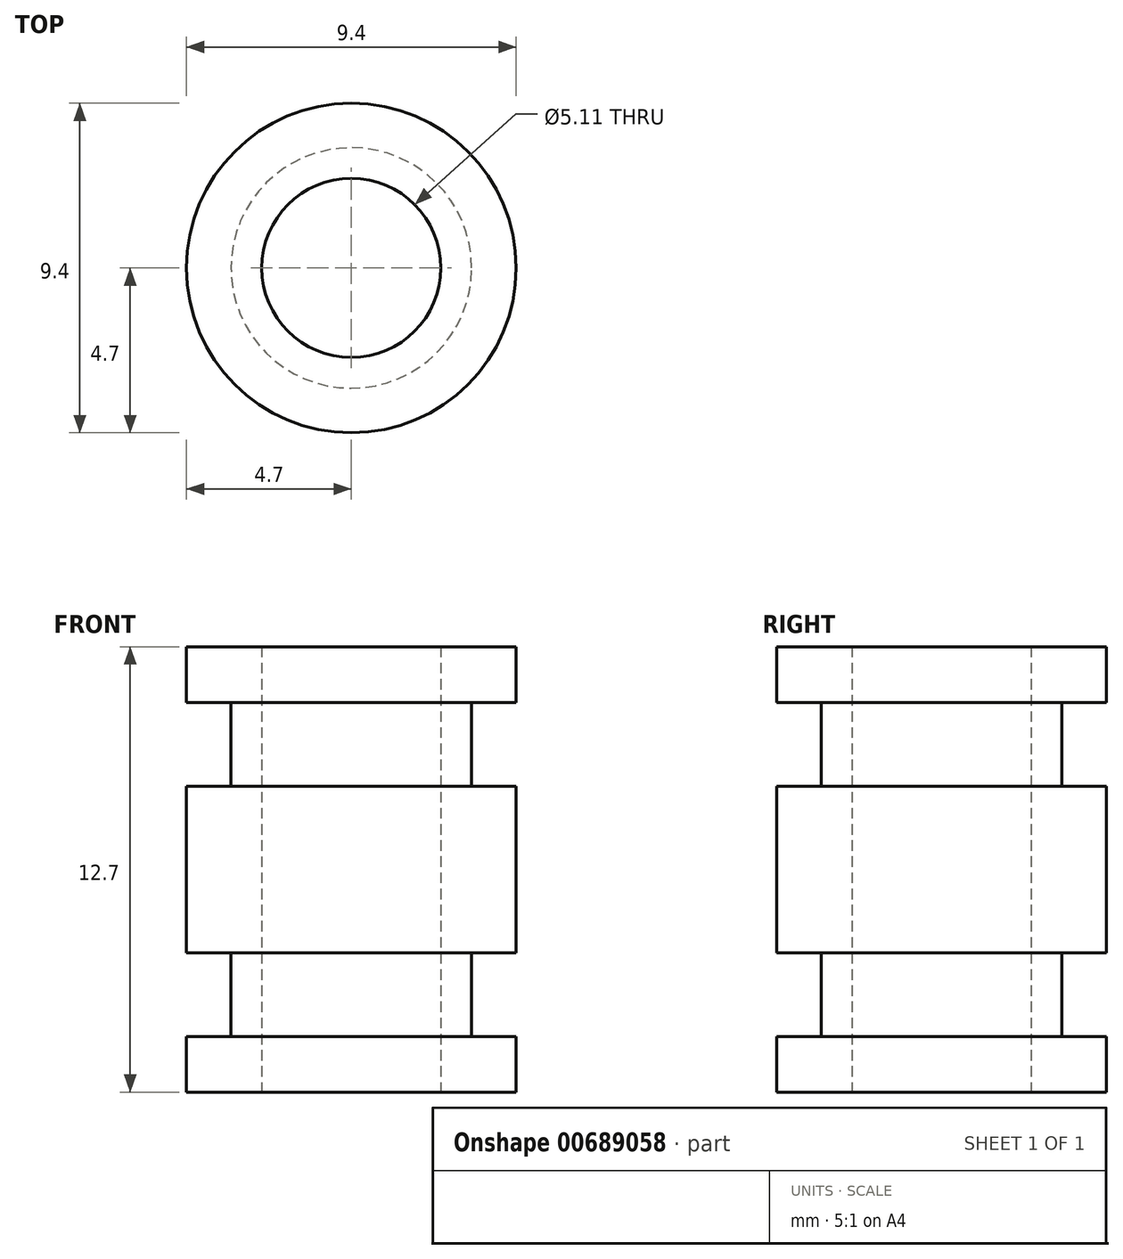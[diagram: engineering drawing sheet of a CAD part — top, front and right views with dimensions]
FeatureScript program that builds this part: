
annotation { "Feature Type Name" : "Feature", "Feature Type Description" : "" }
export const myFeature = defineFeature(function(context is Context, id is Id, definition is map)
    precondition{}
    {
        {
            var Q0;
            Q0=qCreatedBy(makeId("Front.planeOp"),FACE);
            var sketch = newSketch(context, id + "F0", { "sketchPlane" : qUnion([Q0])});
            skPoint(sketch, "E0", {"position": v(0, 6.35) * mm});
            skLineSegment(sketch, "E1", {"start": v(0, 6.35) * mm, "end": v(24.5, 6.35) * mm, "construction": true});
            skLineSegment(sketch, "E2", {"start": v(0, 6.35) * mm, "end": v(0, 0) * mm});
            skLineSegment(sketch, "E3", {"start": v(0, 0) * mm, "end": v(4.7, 0) * mm});
            skLineSegment(sketch, "E4", {"start": v(4.7, 0) * mm, "end": v(4.7, 1.59) * mm});
            skLineSegment(sketch, "E5", {"start": v(4.7, 1.59) * mm, "end": v(3.43, 1.59) * mm});
            skLineSegment(sketch, "E6", {"start": v(3.43, 1.59) * mm, "end": v(3.43, 3.98) * mm});
            skLineSegment(sketch, "E7", {"start": v(3.43, 3.98) * mm, "end": v(4.7, 3.98) * mm});
            skLineSegment(sketch, "E8", {"start": v(4.7, 3.98) * mm, "end": v(4.7, 6.35) * mm});
            skLineSegment(sketch, "E9.MirrorCS", {"start": v(4.7, 8.72) * mm, "end": v(4.7, 6.35) * mm});
            skLineSegment(sketch, "E10.MirrorCS", {"start": v(3.43, 8.72) * mm, "end": v(4.7, 8.72) * mm});
            skLineSegment(sketch, "E11.MirrorCS", {"start": v(3.43, 11.11) * mm, "end": v(3.43, 8.72) * mm});
            skLineSegment(sketch, "E12.MirrorCS", {"start": v(4.7, 11.11) * mm, "end": v(3.43, 11.11) * mm});
            skLineSegment(sketch, "E13.MirrorCS", {"start": v(4.7, 12.7) * mm, "end": v(4.7, 11.11) * mm});
            skLineSegment(sketch, "E14.MirrorCS", {"start": v(0, 12.7) * mm, "end": v(4.7, 12.7) * mm});
            skLineSegment(sketch, "E15", {"start": v(0, 6.35) * mm, "end": v(0, 12.7) * mm});
            skSolve(sketch);
        }
        {
            var Q0;
            Q0=makeQuery(id+"F0.imprint","IMPRINT",FACE,{"disambiguationData":[TD([[makeQuery(id+"F0.imprint","IMPRINT",EDGE,{"derivedFrom":sQuery(id+"F0.wireOp",EDGE,"E2")}),1.0]])]});
            var Q1;
            Q1=sQuery(id+"F0.wireOp",EDGE,"E2");
            revolve(context, id + "F1", {"surfaceOperationType" : NewSurfaceOperationType.NEW, "entities" : qUnion([Q0]), "axis" : qUnion([Q1]), "revolveType" : RevolveType.FULL});
        }
        {
            var Q0;
            Q0=makeQuery(id+"F1.opRevolve","SWEPT_FACE",FACE,{"disambiguationData":[OSD([sQuery(id+"F0.wireOp",EDGE,"E3")])]});
            var sketch = newSketch(context, id + "F2", { "sketchPlane" : qUnion([Q0])});
            skPoint(sketch, "E16", {"position": v(0, 0) * mm});
            skSolve(sketch);
        }
        {
            var Q0;
            Q0=sQuery(id+"F2.wireOp",VERTEX,"E16");
            var Q1;
            Q1=makeQuery(id+"F1.opRevolve","SWEPT_BODY",BODY,{"disambiguationData":[OSD([sQuery(id+"F0.wireOp",EDGE,"E2"),sQuery(id+"F0.wireOp",EDGE,"E3"),sQuery(id+"F0.wireOp",EDGE,"E4"),sQuery(id+"F0.wireOp",EDGE,"E5"),sQuery(id+"F0.wireOp",EDGE,"E6"),sQuery(id+"F0.wireOp",EDGE,"E7"),sQuery(id+"F0.wireOp",EDGE,"E8"),sQuery(id+"F0.wireOp",EDGE,"E9.MirrorCS"),sQuery(id+"F0.wireOp",EDGE,"E10.MirrorCS"),sQuery(id+"F0.wireOp",EDGE,"E11.MirrorCS"),sQuery(id+"F0.wireOp",EDGE,"E12.MirrorCS"),sQuery(id+"F0.wireOp",EDGE,"E13.MirrorCS"),sQuery(id+"F0.wireOp",EDGE,"E14.MirrorCS"),sQuery(id+"F0.wireOp",EDGE,"E15")])]});
            hole(context, id + "F3", {"style" : HoleStyle.SIMPLE, "endStyle" : HoleEndStyle.THROUGH, "standardTappedOrClearance" : lookupTablePath({ "standard" : "ANSI", "engagement" : "75%", "pitch" : "20 tpi", "size" : "1/4", "type" : "Tapped" }), "standardBlindInLast" : lookupTablePath({ "standard" : "ANSI", "engagement" : "75%", "pitch" : "20 tpi", "size" : "1/4", "type" : "Tapped" }), "holeDiameter" : 5.1 * mm, "majorDiameter" : 6.35 * mm, "showTappedDepth" : true, "isTappedThrough" : true, "tappedDepth" : 3 * mm, "tapClearance" : 3, "startFromSketch" : true, "locations" : qUnion([Q0]), "scope" : qUnion([Q1])});
        }
    });
